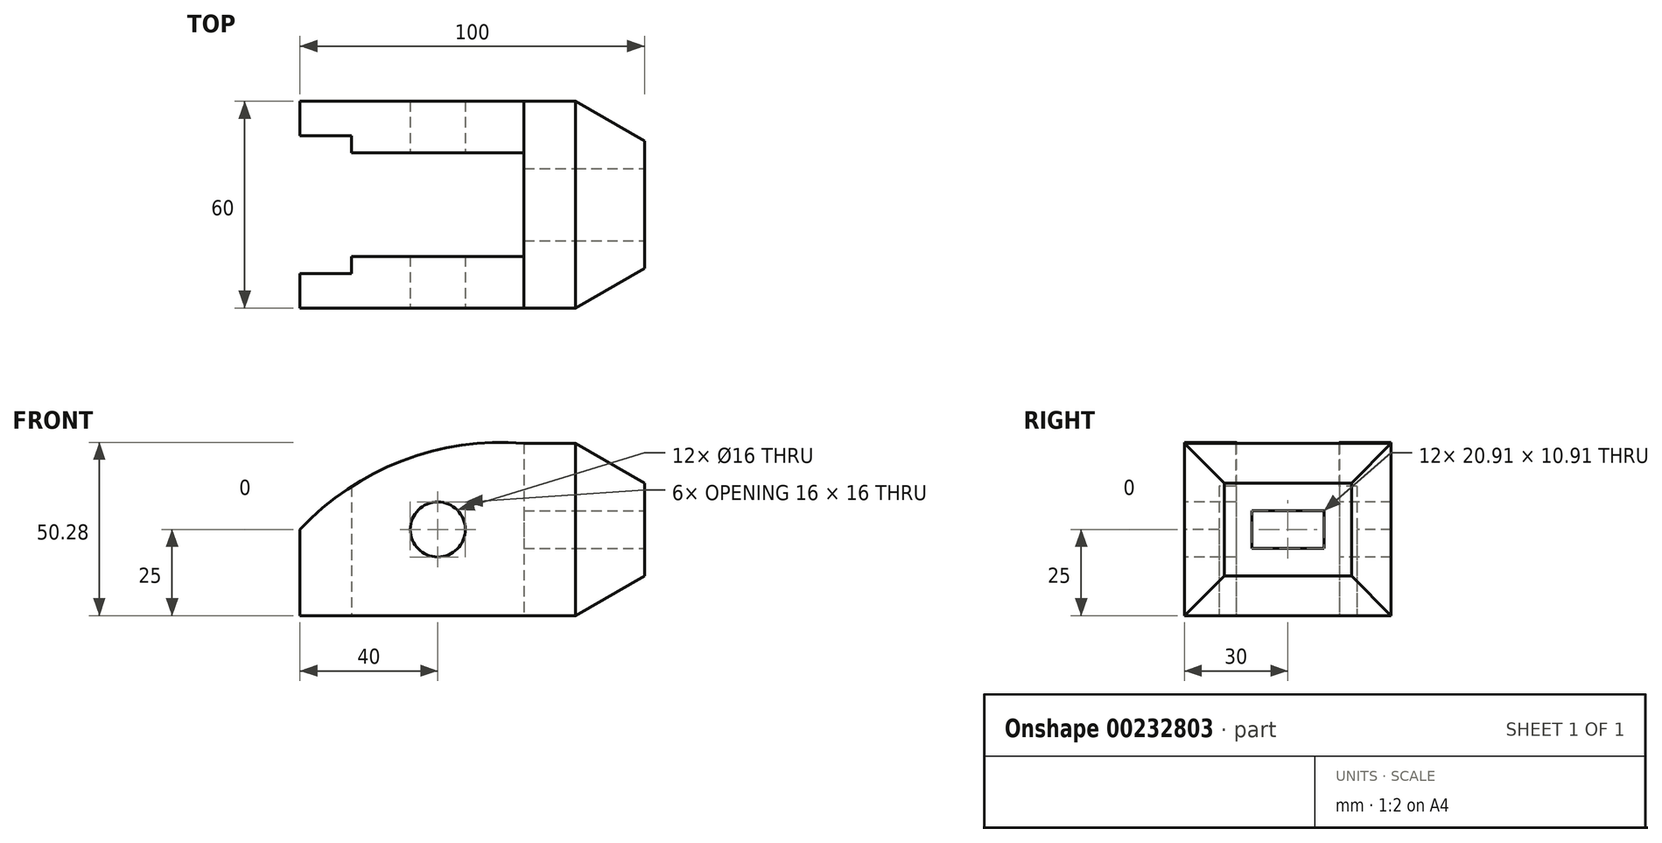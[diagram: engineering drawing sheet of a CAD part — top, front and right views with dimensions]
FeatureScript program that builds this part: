
annotation { "Feature Type Name" : "Feature", "Feature Type Description" : "" }
export const myFeature = defineFeature(function(context is Context, id is Id, definition is map)
    precondition{}
    {
        {
            var Q0;
            Q0=qCreatedBy(makeId("Front.planeOp"),FACE);
            var sketch = newSketch(context, id + "F0", { "sketchPlane" : qUnion([Q0])});
            skLineSegment(sketch, "E0", {"start": v(-80, 0) * mm, "end": v(-80, 25) * mm});
            skLineSegment(sketch, "E1", {"start": v(-80, 0) * mm, "end": v(0, 0) * mm});
            skLineSegment(sketch, "E2", {"start": v(0, 0) * mm, "end": v(0, 50) * mm});
            skLineSegment(sketch, "E3", {"start": v(0, 50) * mm, "end": v(-15, 50) * mm});
            skArc(sketch, "E4", {"start": v(-15, 50) * mm, "mid": v(-50.36, 44.94) * mm, "end": v(-80, 25) * mm});
            skCircle(sketch, "E5", {"center": v(-40, 25) * mm, "radius": 8 * mm});
            skLineSegment(sketch, "E6", {"start": v(0, 0) * mm, "end": v(20, 11.55) * mm});
            skLineSegment(sketch, "E7", {"start": v(20, 11.55) * mm, "end": v(20, 38.45) * mm});
            skLineSegment(sketch, "E8", {"start": v(20, 38.45) * mm, "end": v(0, 50) * mm});
            skSolve(sketch);
        }
        {
            var Q0;
            Q0=makeQuery(id+"F0.imprint","IMPRINT",FACE,{"disambiguationData":[TD([[makeQuery(id+"F0.imprint","IMPRINT",EDGE,{"derivedFrom":sQuery(id+"F0.wireOp",EDGE,"E0")}),-1.0]])]});
            extrude(context, id + "F1", {"entities" : qUnion([Q0]), "oppositeDirection" : true, "depth" : 60 * mm});
        }
        {
            var Q0;
            Q0=makeQuery(id+"F1.opExtrude","SWEPT_FACE",FACE,{"disambiguationData":[OSD([sQuery(id+"F0.wireOp",EDGE,"E1")])]});
            var sketch = newSketch(context, id + "F2", { "sketchPlane" : qUnion([Q0])});
            skLineSegment(sketch, "E9.bottom", {"start": v(-65, -50) * mm, "end": v(-80, -50) * mm});
            skLineSegment(sketch, "E9.top", {"start": v(-65, -10) * mm, "end": v(-80, -10) * mm});
            skLineSegment(sketch, "E9.left", {"start": v(-65, -50) * mm, "end": v(-65, -10) * mm});
            skLineSegment(sketch, "E9.right", {"start": v(-80, -50) * mm, "end": v(-80, -10) * mm});
            skLineSegment(sketch, "E10.bottom", {"start": v(-65, -15) * mm, "end": v(-15, -15) * mm});
            skLineSegment(sketch, "E10.top", {"start": v(-65, -45) * mm, "end": v(-15, -45) * mm});
            skLineSegment(sketch, "E10.left", {"start": v(-65, -15) * mm, "end": v(-65, -45) * mm});
            skLineSegment(sketch, "E10.right", {"start": v(-15, -15) * mm, "end": v(-15, -45) * mm});
            skLineSegment(sketch, "E11.0.0", {"start": v(0, 0) * mm, "end": v(-80, 0) * mm, "construction": true});
            skLineSegment(sketch, "E11.0.1", {"start": v(-80, 0) * mm, "end": v(-80, -60) * mm, "construction": true});
            skLineSegment(sketch, "E11.0.2", {"start": v(-80, -60) * mm, "end": v(0, -60) * mm, "construction": true});
            skLineSegment(sketch, "E11.0.3", {"start": v(0, -60) * mm, "end": v(0, 0) * mm, "construction": true});
            skLineSegment(sketch, "E12.0", {"start": v(20, 0) * mm, "end": v(0, 0) * mm, "construction": true});
            skPoint(sketch, "E13.0", {"position": v(20, 0) * mm});
            skPoint(sketch, "E14.0", {"position": v(0, 0) * mm});
            skSolve(sketch);
        }
        {
            var Q0;
            {var subQ3=sQuery(id+"F2.wireOp",EDGE,"E9.bottom");Q0=makeQuery(id+"F2.imprint","IMPRINT",FACE,{"disambiguationData":[TD([[makeQuery(id+"F2.imprint","IMPRINT",EDGE,{"derivedFrom":subQ3}),-1.0]])]});}
            var Q1;
            Q1=makeQuery(id+"F2.imprint","IMPRINT",FACE,{"disambiguationData":[TD([[makeQuery(id+"F2.imprint","IMPRINT",EDGE,{"derivedFrom":sQuery(id+"F2.wireOp",EDGE,"E10.bottom")}),-1.0]])]});
            extrude(context, id + "F3", {"entities" : qUnion([Q0, Q1]), "operationType" : NewBodyOperationType.REMOVE, "endBound" : BoundingType.THROUGH_ALL, "oppositeDirection" : true, "depth" : 25 * mm});
        }
        {
            var Q0;
            Q0=makeQuery(id+"F0.imprint","IMPRINT",FACE,{"disambiguationData":[TD([[makeQuery(id+"F0.imprint","IMPRINT",EDGE,{"derivedFrom":sQuery(id+"F0.wireOp",EDGE,"E2")}),-1.0]])]});
            extrude(context, id + "F4", {"entities" : qUnion([Q0]), "oppositeDirection" : true, "depth" : 60 * mm});
        }
        {
            var Q0;
            Q0=qCreatedBy(makeId("Top.planeOp"),FACE);
            var sketch = newSketch(context, id + "F5", { "sketchPlane" : qUnion([Q0])});
            skLineSegment(sketch, "E15.0.1", {"start": v(0, 0) * mm, "end": v(0, 60) * mm, "construction": true});
            skLineSegment(sketch, "E16.0.0", {"start": v(20, 0) * mm, "end": v(0, 0) * mm, "construction": true});
            skLineSegment(sketch, "E16.0.2", {"start": v(0, 60) * mm, "end": v(20, 60) * mm, "construction": true});
            skLineSegment(sketch, "E16.0.3", {"start": v(20, 60) * mm, "end": v(20, 0) * mm, "construction": true});
            skLineSegment(sketch, "E17", {"start": v(0, 0) * mm, "end": v(20, 0) * mm});
            skLineSegment(sketch, "E18", {"start": v(0, 0) * mm, "end": v(20, 11.55) * mm});
            skLineSegment(sketch, "E19", {"start": v(20, 11.55) * mm, "end": v(20, 0) * mm});
            skLineSegment(sketch, "E20", {"start": v(0, 60) * mm, "end": v(20, 48.45) * mm});
            skLineSegment(sketch, "E21", {"start": v(20, 48.45) * mm, "end": v(20, 60) * mm});
            skLineSegment(sketch, "E22", {"start": v(0, 60) * mm, "end": v(20, 60) * mm});
            skSolve(sketch);
        }
        {
            var Q0;
            Q0=makeQuery(id+"F5.imprint","IMPRINT",FACE,{"disambiguationData":[TD([[makeQuery(id+"F5.imprint","IMPRINT",EDGE,{"derivedFrom":sQuery(id+"F5.wireOp",EDGE,"E17")}),1.0]])]});
            var Q1;
            Q1=makeQuery(id+"F5.imprint","IMPRINT",FACE,{"disambiguationData":[TD([[makeQuery(id+"F5.imprint","IMPRINT",EDGE,{"derivedFrom":sQuery(id+"F5.wireOp",EDGE,"E20")}),1.0]])]});
            extrude(context, id + "F6", {"entities" : qUnion([Q0, Q1]), "operationType" : NewBodyOperationType.REMOVE, "endBound" : BoundingType.THROUGH_ALL, "depth" : 25 * mm});
        }
        {
            var Q0;
            Q0=makeQuery(id+"F4.opExtrude","SWEPT_FACE",FACE,{"disambiguationData":[OSD([sQuery(id+"F0.wireOp",EDGE,"E7")])]});
            var sketch = newSketch(context, id + "F7", { "sketchPlane" : qUnion([Q0])});
            skLineSegment(sketch, "E23.0.0", {"start": v(48.45, 38.45) * mm, "end": v(11.55, 38.45) * mm});
            skLineSegment(sketch, "E23.0.1", {"start": v(11.55, 38.45) * mm, "end": v(11.55, 11.55) * mm});
            skLineSegment(sketch, "E23.0.2", {"start": v(11.55, 11.55) * mm, "end": v(48.45, 11.55) * mm});
            skLineSegment(sketch, "E23.0.3", {"start": v(48.45, 11.55) * mm, "end": v(48.45, 38.45) * mm});
            skLineSegment(sketch, "E24.0", {"start": v(40.45, 30.45) * mm, "end": v(19.55, 30.45) * mm});
            skLineSegment(sketch, "E24.1", {"start": v(40.45, 19.55) * mm, "end": v(40.45, 30.45) * mm});
            skLineSegment(sketch, "E24.2", {"start": v(19.55, 19.55) * mm, "end": v(40.45, 19.55) * mm});
            skLineSegment(sketch, "E24.3", {"start": v(19.55, 30.45) * mm, "end": v(19.55, 19.55) * mm});
            skSolve(sketch);
        }
        {
            var Q0;
            Q0=makeQuery(id+"F7.imprint","IMPRINT",FACE,{"disambiguationData":[TD([[makeQuery(id+"F7.imprint","IMPRINT",EDGE,{"derivedFrom":sQuery(id+"F7.wireOp",EDGE,"E24.0")}),1.0]])]});
            extrude(context, id + "F8", {"entities" : qUnion([Q0]), "operationType" : NewBodyOperationType.REMOVE, "endBound" : BoundingType.THROUGH_ALL, "oppositeDirection" : true, "depth" : 25 * mm});
        }
    });
